# Revit family: Lighting-Pendant-Amerlux-Linea 1.5
name_source: partatom
category: Lighting Fixtures
revit_build: Autodesk Revit Architecture 2012 (Build: 20110916_2132(x64)
units: mm (PartAtom-declared; Revit-internal decimal feet)

## types (4) — shared parameters
Apparent Load = 0 VA
Color Filter = 16777215
Default Elevation = 4' - 0"
Description = Linear Pendant
Dimming Lamp Color Temperature Shift = <None>
Emit Shape Visible in Rendering = Yes
Emit from Rectangle Length = 4' - 0"
Emit from Rectangle Width = 0' - 1 1/2"
IES File Link = http://www.amerlux.com
Length = 4' - 0"
Manufacturer = Amerlux
Model = Linea 1.5"
Number of Poles = 1
Power Factor = 1
Tilt Angle = -90.00°
URL = http://www.amerlux.com
Voltage = 0 V
Width = 0' - 1 1/2"

## per-type parameters (varying)
| type | Height |
| Direct/Indirect | 0' - 3 1/4" |
| Direct | 0' - 3 1/4" |
| Indirect | 0' - 3 1/4" |
| Remote Driver | 0' - 1 7/8" |

## geometry (parser evidence)
native form markers: Blend x10, Sweep x1
no freeform markers — native parametric forms only
